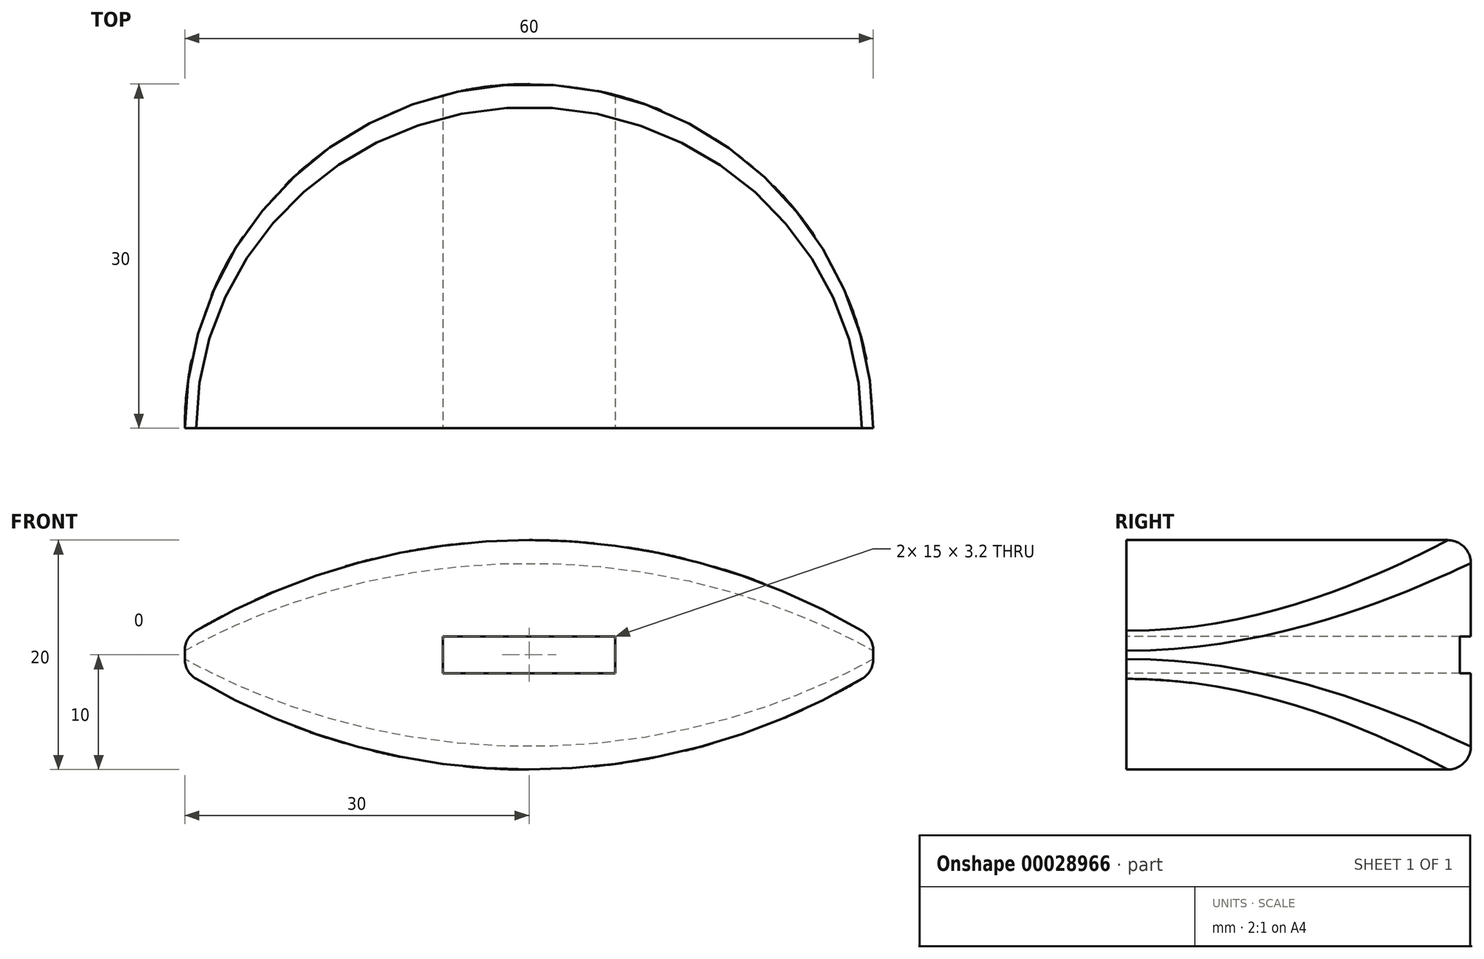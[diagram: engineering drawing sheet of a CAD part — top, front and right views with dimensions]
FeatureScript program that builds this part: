
annotation { "Feature Type Name" : "Feature", "Feature Type Description" : "" }
export const myFeature = defineFeature(function(context is Context, id is Id, definition is map)
    precondition{}
    {
        {
            var Q0;
            Q0=qCreatedBy(makeId("Top.planeOp"),FACE);
            var sketch = newSketch(context, id + "F0", { "sketchPlane" : qUnion([Q0])});
            skLineSegment(sketch, "E0", {"start": v(0, 0) * mm, "end": v(0, 30) * mm, "construction": true});
            skLineSegment(sketch, "E1", {"start": v(0, 0) * mm, "end": v(-30, 0) * mm});
            skLineSegment(sketch, "E2.MirrorCS", {"start": v(0, 0) * mm, "end": v(30, 0) * mm});
            skArc(sketch, "E3", {"start": v(30, 0) * mm, "mid": v(0, 30) * mm, "end": v(-30, 0) * mm});
            skSolve(sketch);
        }
        {
            var Q0;
            Q0=makeQuery(id+"F0.imprint","IMPRINT",FACE,{"disambiguationData":[TD([[makeQuery(id+"F0.imprint","IMPRINT",EDGE,{"derivedFrom":sQuery(id+"F0.wireOp",EDGE,"E1")}),-1.0]])]});
            extrude(context, id + "F1", {"entities" : qUnion([Q0]), "depth" : 25 * mm});
        }
        {
            var Q0;
            Q0=makeQuery(id+"F1.opExtrude","SWEPT_FACE",FACE,{"disambiguationData":[OSD([sQuery(id+"F0.wireOp",EDGE,"E1"),sQuery(id+"F0.wireOp",EDGE,"E2.MirrorCS")])]});
            var sketch = newSketch(context, id + "F2", { "sketchPlane" : qUnion([Q0])});
            skLineSegment(sketch, "E4.0.0", {"start": v(-30, 0) * mm, "end": v(30, 0) * mm});
            skLineSegment(sketch, "E4.0.1", {"start": v(30, 0) * mm, "end": v(30, 25) * mm});
            skLineSegment(sketch, "E4.0.2", {"start": v(30, 25) * mm, "end": v(-30, 25) * mm});
            skLineSegment(sketch, "E4.0.3", {"start": v(-30, 25) * mm, "end": v(-30, 0) * mm});
            skPoint(sketch, "E5", {"position": v(30, 12.5) * mm});
            skPoint(sketch, "E6", {"position": v(0, 12.5) * mm});
            skPoint(sketch, "E7", {"position": v(0, 0) * mm});
            skPoint(sketch, "E8", {"position": v(0, 25) * mm});
            skLineSegment(sketch, "E9", {"start": v(30, 12.5) * mm, "end": v(30, 14) * mm, "construction": true});
            skPoint(sketch, "E10", {"position": v(0, 22.5) * mm});
            skPoint(sketch, "E11.MirrorP", {"position": v(-30, 12.5) * mm});
            skPoint(sketch, "E12", {"position": v(30, 14) * mm});
            skPoint(sketch, "E13.MirrorP", {"position": v(-30, 14) * mm});
            skArc(sketch, "E14", {"start": v(30, 14) * mm, "mid": v(0, 22.5) * mm, "end": v(-30, 14) * mm});
            skLineSegment(sketch, "E15", {"start": v(-30, 12.5) * mm, "end": v(30, 12.5) * mm, "construction": true});
            skPoint(sketch, "E16.MirrorP", {"position": v(-30, 11) * mm});
            skPoint(sketch, "E17.MirrorP", {"position": v(30, 11) * mm});
            skPoint(sketch, "E18.MirrorP", {"position": v(0, 2.5) * mm});
            skArc(sketch, "E19", {"start": v(-30, 11) * mm, "mid": v(0, 2.5) * mm, "end": v(30, 11) * mm});
            skLineSegment(sketch, "E20", {"start": v(-30, 14) * mm, "end": v(-30, 11) * mm});
            skLineSegment(sketch, "E21", {"start": v(30, 14) * mm, "end": v(30, 11) * mm});
            skPoint(sketch, "E22", {"position": v(-7.5, 14.1) * mm});
            skPoint(sketch, "E23.MirrorP", {"position": v(-7.5, 10.9) * mm});
            skLineSegment(sketch, "E24.MirrorCS", {"start": v(0, 25) * mm, "end": v(0, 0) * mm, "construction": true});
            skPoint(sketch, "E25.MirrorP", {"position": v(7.5, 14.1) * mm});
            skPoint(sketch, "E26.MirrorP", {"position": v(7.5, 10.9) * mm});
            skLineSegment(sketch, "E27", {"start": v(-7.5, 14.1) * mm, "end": v(7.5, 14.1) * mm});
            skLineSegment(sketch, "E28", {"start": v(7.5, 14.1) * mm, "end": v(7.5, 10.9) * mm});
            skLineSegment(sketch, "E29", {"start": v(-7.5, 10.9) * mm, "end": v(-7.5, 14.1) * mm});
            skLineSegment(sketch, "E30", {"start": v(-7.5, 10.9) * mm, "end": v(7.5, 10.9) * mm});
            skSolve(sketch);
        }
        {
            var Q0;
            {var subQ2=sQuery(id+"F2.wireOp",EDGE,"E4.0.2");Q0=makeQuery(id+"F2.imprint","IMPRINT",FACE,{"disambiguationData":[TD([[makeQuery(id+"F2.imprint","IMPRINT",EDGE,{"derivedFrom":subQ2}),1.0]])]});}
            var Q1;
            {var subQ2=sQuery(id+"F2.wireOp",EDGE,"E4.0.0");Q1=makeQuery(id+"F2.imprint","IMPRINT",FACE,{"disambiguationData":[TD([[makeQuery(id+"F2.imprint","IMPRINT",EDGE,{"derivedFrom":subQ2}),-1.0]])]});}
            var Q2;
            Q2=makeQuery(id+"F2.imprint","IMPRINT",FACE,{"disambiguationData":[TD([[makeQuery(id+"F2.imprint","IMPRINT",EDGE,{"derivedFrom":sQuery(id+"F2.wireOp",EDGE,"E27")}),-1.0]])]});
            extrude(context, id + "F3", {"entities" : qUnion([Q0, Q1, Q2]), "operationType" : NewBodyOperationType.REMOVE, "oppositeDirection" : true, "depth" : 30 * mm});
        }
        {
            var Q0;
            Q0=makeQuery(id+"F3.boolean.opBoolean","INTERSECT",EDGE,{"derivedFrom":[makeQuery(id+"F1.opExtrude","SWEPT_FACE",FACE,{"disambiguationData":[OSD([sQuery(id+"F0.wireOp",EDGE,"E3")])]}),makeQuery(id+"F3.opExtrude","SWEPT_FACE",FACE,{"disambiguationData":[OSD([sQuery(id+"F2.wireOp",EDGE,"E19")])]})]});
            var Q1;
            Q1=makeQuery(id+"F3.boolean.opBoolean","INTERSECT",EDGE,{"derivedFrom":[makeQuery(id+"F1.opExtrude","SWEPT_FACE",FACE,{"disambiguationData":[OSD([sQuery(id+"F0.wireOp",EDGE,"E3")])]}),makeQuery(id+"F3.opExtrude","SWEPT_FACE",FACE,{"disambiguationData":[OSD([sQuery(id+"F2.wireOp",EDGE,"E14")])]})]});
            fillet(context, id + "F4", {"entities" : qUnion([Q0, Q1]), "radius" : 2 * mm, "tangentPropagation" : true, "allowEdgeOverflow" : false});
        }
    });
